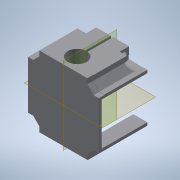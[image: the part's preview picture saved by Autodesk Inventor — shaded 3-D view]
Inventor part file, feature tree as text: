
AUTODESK INVENTOR PART (.ipt)
format: ipt  version: 2022 (Build 260153000, 153)  size: 386,048 bytes
history: native  units: mm
features: extrude x13, sketch x13, plane x10, projected_geometry x5, hole x1, pattern_circular x1
ambient origin geometry x8: Origin, YZ Plane, XZ Plane, XY Plane, X Axis, Y Axis, Z Axis, Center Point
bodies: Body1 (feature_tree)
feature tree (43):
  plane  "Work Plane1"
  plane  "Work Plane2"
  plane  "Work Plane4"
  extrude  "Extrusion1"  Depth=24.9mm
  extrude  "IM_offset"  Depth=26.9mm
  plane  "Work Plane3"
  sketch  "Sketch9"  dims[d5=20.0mm d6=4.0mm d7=0.0mm]
  plane  "Work Plane5"
  plane  "Work Plane10"
  extrude  "Extrusion9"  Depth=4.0mm TaperAngle=0.0deg
  plane  "Work Plane6"
  plane  "Work Plane7"
  extrude  "Extrusion11"  Depth=0.2mm TaperAngle=0.0deg
  plane  "Work Plane8"
  plane  "Work Plane9"
  extrude  "Extrusion12"  Depth=2.0mm TaperAngle=360.0deg
  hole  "Hole2"  [1 undecoded]
  extrude  "Extrusion14"  Depth=10.0mm TaperAngle=0.0deg
  extrude  "Extrusion15"  Depth=3.0mm
  extrude  "Extrusion16"  Depth=10.0mm TaperAngle=0.0deg
  extrude  "Extrusion17"  Depth=10.0mm TaperAngle=0.0deg
  pattern_circular  "Circular Pattern1"  Count=2 Angle=90.0deg
  extrude  "Extrusion18"  Depth=10.0mm TaperAngle=0.0deg
  extrude  "Extrusion19"  Depth=10.0mm TaperAngle=0.0deg
  extrude  "Extrusion20"  Depth=2.0mm TaperAngle=0.0deg
  extrude  "Extrusion21"  Depth=2.0mm
  sketch  "Sketch1"  dims[d0=45.0deg d2=24.9mm]
  sketch  "Skizze6"  dims[d3=3.14mm d4=26.9mm]
  projected_geometry  "Projizierte Kontur2"
  projected_geometry  "Projected Loop5"
  sketch  "Sketch12"  dims[d25=0.2mm d26=1.0mm d27=0.0mm]
  projected_geometry  "Projected Loop6"
  sketch  "Sketch14"  dims[d44=2.0mm d45=40.0mm d47=360.0deg]
  sketch  "Sketch15"  dims[d49=10.0mm d50=0.0mm d53=10.0mm d54=0.0mm]
  sketch  "Sketch16"  dims[d55=10.0mm d56=0.0mm]
  sketch  "Sketch17"  dims[d60=2.9mm d61=6.0mm d62=6.0mm d63=3.0mm d64=90.0deg d65=12.0mm d66=20.594885mm d67=10.0mm d68=6.0mm d69=0.0mm d70=0.0mm]
  projected_geometry  "Projected Loop8"
  sketch  "Sketch18"  dims[d71=3.0mm d72=3.0mm]
  projected_geometry  "Projected Loop9"
  sketch  "Sketch19"  dims[d74=10.0mm d75=0.0mm d77=10.0mm d78=0.0mm]
  sketch  "Sketch20"  dims[d79=1.0mm d80=10.0mm d81=0.0mm d82=20.0mm d83=90.0deg]
  sketch  "Sketch22"  dims[d85=1.5mm d86=10.0mm d87=0.0mm]
  sketch  "Sketch23"  dims[d93=0.8mm d94=10.0mm d95=0.0mm d97=2.0mm d98=0.0mm d99=0.15mm d100=0.0mm d101=0.0mm d102=12.8mm d103=12.8mm]
note: 1 required parameter value undecoded (feature->parameter linkage not recoverable at this tier; creation-order binding heuristic only, values carry confidence <= 0.55)
